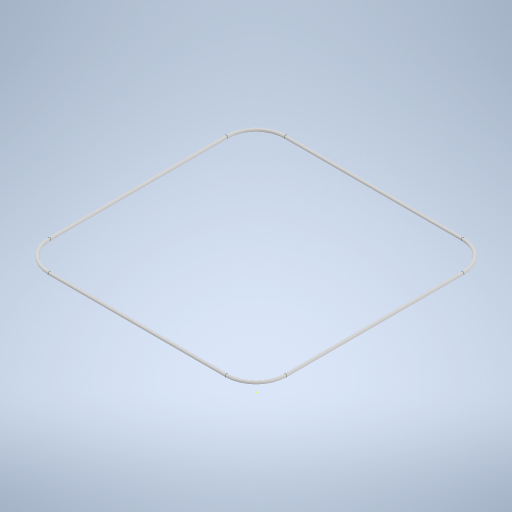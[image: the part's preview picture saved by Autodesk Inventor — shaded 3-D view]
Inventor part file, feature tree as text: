
AUTODESK INVENTOR PART (.ipt)
format: ipt  version: 2024 (Build 280153000, 153)  size: 267,776 bytes
history: native  units: mm
features: sketch x3, other x1, plane x1, sweep x1
ambient origin geometry x8: Origin, YZ Plane, XZ Plane, XY Plane, X Axis, Y Axis, Z Axis, Center Point
bodies: Body1 (feature_tree)
feature tree (6):
  other  "Sólido1"
  sketch  "Boceto1"  dims[d0=4000.0mm d1=4000.0mm]
  sketch  "Boceto 3D1"  dims[d2=4000.0mm]
  plane  "Plano de trabajo1"
  sweep  "Barrido1"
  sketch  "Boceto2"  dims[d3=500.0mm d5=500.0mm d6=500.0mm d7=3000.0mm d8=995.0mm d9=500.0mm d10=500.0mm d11=50.0mm d12=0.0mm d13=0.0mm]
